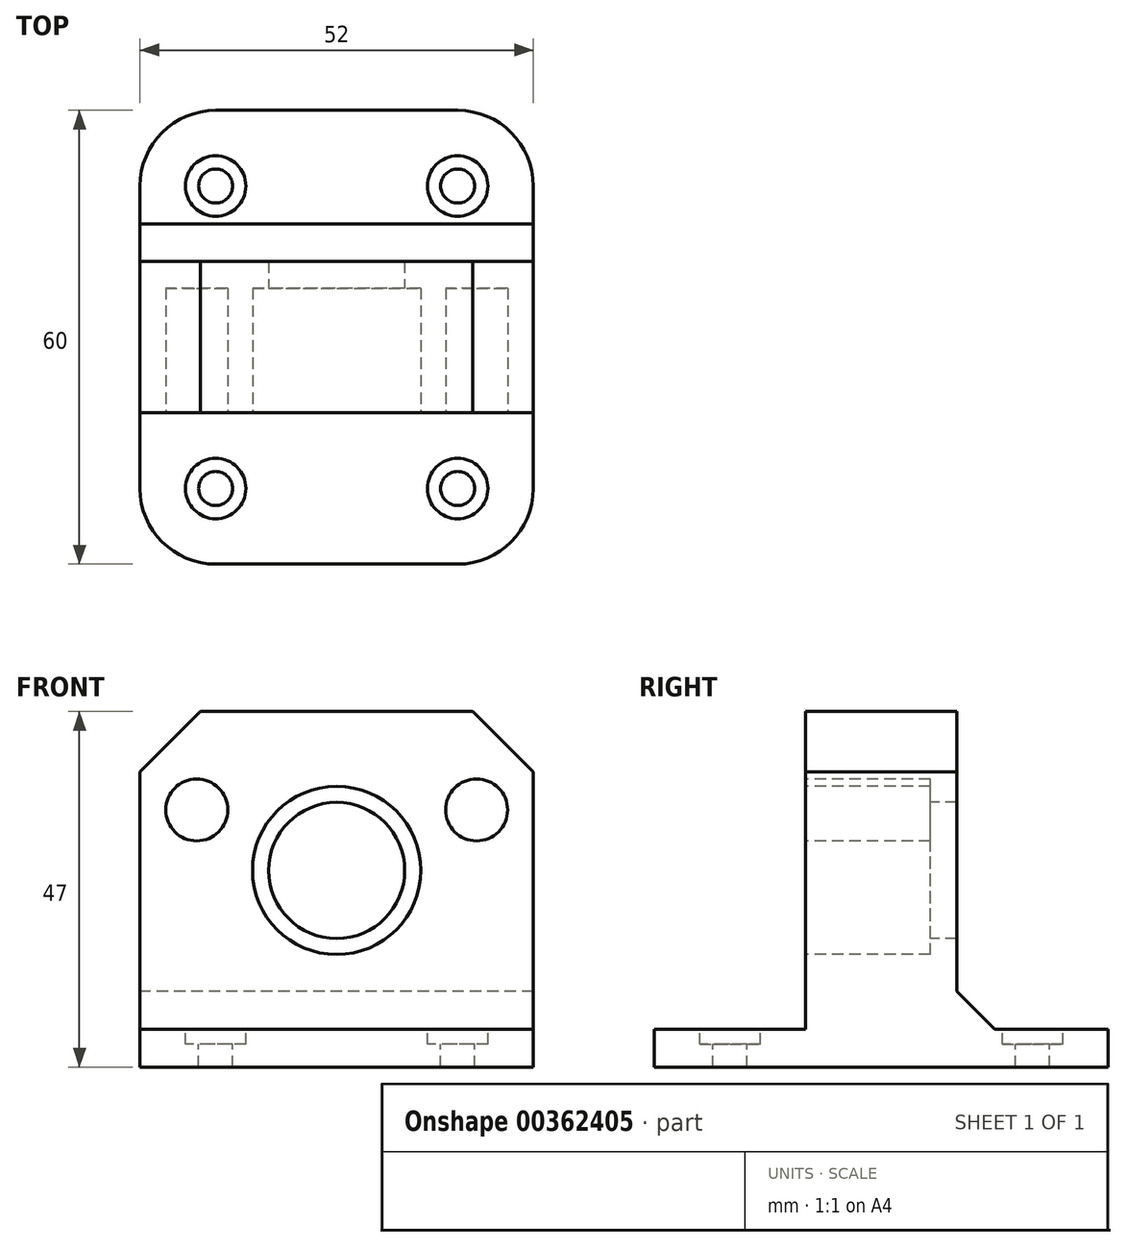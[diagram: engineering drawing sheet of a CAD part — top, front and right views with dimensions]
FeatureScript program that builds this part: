
annotation { "Feature Type Name" : "Feature", "Feature Type Description" : "" }
export const myFeature = defineFeature(function(context is Context, id is Id, definition is map)
    precondition{}
    {
        {
            var Q0;
            Q0=qCreatedBy(makeId("Front.planeOp"),FACE);
            var sketch = newSketch(context, id + "F0", { "sketchPlane" : qUnion([Q0])});
            skLineSegment(sketch, "E0.bottom", {"start": v(26, -21) * mm, "end": v(-26, -21) * mm});
            skLineSegment(sketch, "E0.top", {"start": v(26, 21) * mm, "end": v(-26, 21) * mm});
            skLineSegment(sketch, "E0.left", {"start": v(26, -21) * mm, "end": v(26, 21) * mm});
            skLineSegment(sketch, "E0.right", {"start": v(-26, -21) * mm, "end": v(-26, 21) * mm});
            skPoint(sketch, "E0.middle", {"position": v(0, 0) * mm});
            skSolve(sketch);
        }
        {
            var Q0;
            Q0=qSketchRegion(id+"F0",true);
            extrude(context, id + "F1", {"entities" : qUnion([Q0]), "endBound" : BoundingType.SYMMETRIC, "depth" : 20 * mm});
        }
        {
            var Q0;
            Q0=qCreatedBy(makeId("Front.planeOp"),FACE);
            var sketch = newSketch(context, id + "F2", { "sketchPlane" : qUnion([Q0])});
            skLineSegment(sketch, "E1.bottom", {"start": v(-26, -21) * mm, "end": v(26, -21) * mm});
            skLineSegment(sketch, "E1.top", {"start": v(-26, -26) * mm, "end": v(26, -26) * mm});
            skLineSegment(sketch, "E1.left", {"start": v(-26, -21) * mm, "end": v(-26, -26) * mm});
            skLineSegment(sketch, "E1.right", {"start": v(26, -21) * mm, "end": v(26, -26) * mm});
            skSolve(sketch);
        }
        {
            var Q0;
            Q0=qSketchRegion(id+"F2",true);
            extrude(context, id + "F3", {"entities" : qUnion([Q0]), "operationType" : NewBodyOperationType.ADD, "endBound" : BoundingType.SYMMETRIC, "depth" : 60 * mm});
        }
        {
            var Q0;
            Q0=makeQuery(id+"F1.opExtrude","CAP_FACE",FACE,{"disambiguationData":[OSD([sQuery(id+"F0.wireOp",EDGE,"E0.bottom"),sQuery(id+"F0.wireOp",EDGE,"E0.top"),sQuery(id+"F0.wireOp",EDGE,"E0.left"),sQuery(id+"F0.wireOp",EDGE,"E0.right")])],"isStart":false});
            var sketch = newSketch(context, id + "F4", { "sketchPlane" : qUnion([Q0])});
            skCircle(sketch, "E2", {"center": v(0, 0) * mm, "radius": 9 * mm});
            skSolve(sketch);
        }
        {
            var Q0;
            Q0=qSketchRegion(id+"F4",true);
            extrude(context, id + "F5", {"entities" : qUnion([Q0]), "operationType" : NewBodyOperationType.REMOVE, "endBound" : BoundingType.THROUGH_ALL, "oppositeDirection" : true, "depth" : 25 * mm});
        }
        {
            var Q0;
            Q0=makeQuery(id+"F1.opExtrude","CAP_FACE",FACE,{"disambiguationData":[OSD([sQuery(id+"F0.wireOp",EDGE,"E0.bottom"),sQuery(id+"F0.wireOp",EDGE,"E0.top"),sQuery(id+"F0.wireOp",EDGE,"E0.left"),sQuery(id+"F0.wireOp",EDGE,"E0.right")])],"isStart":false});
            var sketch = newSketch(context, id + "F6", { "sketchPlane" : qUnion([Q0])});
            skCircle(sketch, "E3", {"center": v(0, 0) * mm, "radius": 11.12 * mm});
            skCircle(sketch, "E4", {"center": v(-18.5, 8) * mm, "radius": 4.1 * mm});
            skCircle(sketch, "E5", {"center": v(18.5, 8) * mm, "radius": 4.1 * mm});
            skSolve(sketch);
        }
        {
            var Q0;
            Q0=qSketchRegion(id+"F6",true);
            extrude(context, id + "F7", {"entities" : qUnion([Q0]), "operationType" : NewBodyOperationType.REMOVE, "oppositeDirection" : true, "depth" : 16.5 * mm});
        }
        {
            var Q0;
            {var subQ2=sQuery(id+"F2.wireOp",EDGE,"E1.bottom");var subQ3=sQuery(id+"F0.wireOp",EDGE,"E0.right");var subQ4=sQuery(id+"F0.wireOp",EDGE,"E0.left");Q0=makeQuery(id+"F3.boolean.opBoolean","SPLIT",FACE,{"disambiguationData":[TD([makeQuery(id+"F1.opExtrude","CAP_FACE",FACE,{"disambiguationData":[OSD([sQuery(id+"F0.wireOp",EDGE,"E0.bottom"),sQuery(id+"F0.wireOp",EDGE,"E0.top"),subQ4,subQ3])],"isStart":false})])],"derivedFrom":makeQuery(id+"F3.opExtrude","SWEPT_FACE",FACE,{"disambiguationData":[OSD([subQ2])]})});}
            var sketch = newSketch(context, id + "F8", { "sketchPlane" : qUnion([Q0])});
            skCircle(sketch, "E6", {"center": v(-16, 20) * mm, "radius": 2.25 * mm});
            skCircle(sketch, "E7", {"center": v(16, 20) * mm, "radius": 2.25 * mm});
            skCircle(sketch, "E8", {"center": v(16, -20) * mm, "radius": 2.25 * mm});
            skCircle(sketch, "E9", {"center": v(-16, -20) * mm, "radius": 2.25 * mm});
            skSolve(sketch);
        }
        {
            var Q0;
            Q0=qSketchRegion(id+"F8",true);
            extrude(context, id + "F9", {"entities" : qUnion([Q0]), "operationType" : NewBodyOperationType.REMOVE, "endBound" : BoundingType.THROUGH_ALL, "oppositeDirection" : true, "depth" : 25 * mm});
        }
        {
            var Q0;
            {var subQ0=sQuery(id+"F0.wireOp",EDGE,"E0.right");var subQ1=sQuery(id+"F0.wireOp",EDGE,"E0.left");var subQ4=sQuery(id+"F2.wireOp",EDGE,"E1.bottom");Q0=makeQuery(id+"F3.boolean.opBoolean","SPLIT",FACE,{"disambiguationData":[TD([makeQuery(id+"F1.opExtrude","CAP_FACE",FACE,{"disambiguationData":[OSD([sQuery(id+"F0.wireOp",EDGE,"E0.bottom"),sQuery(id+"F0.wireOp",EDGE,"E0.top"),subQ1,subQ0])],"isStart":true})])],"derivedFrom":makeQuery(id+"F3.opExtrude","SWEPT_FACE",FACE,{"disambiguationData":[OSD([subQ4])]})});}
            var sketch = newSketch(context, id + "F10", { "sketchPlane" : qUnion([Q0])});
            skCircle(sketch, "E10", {"center": v(-16, 20) * mm, "radius": 4 * mm});
            skCircle(sketch, "E11", {"center": v(16, 20) * mm, "radius": 4 * mm});
            skCircle(sketch, "E12", {"center": v(-16, -20) * mm, "radius": 4 * mm});
            skCircle(sketch, "E13", {"center": v(16, -20) * mm, "radius": 4 * mm});
            skSolve(sketch);
        }
        {
            var Q0;
            Q0=qSketchRegion(id+"F10",true);
            extrude(context, id + "F11", {"entities" : qUnion([Q0]), "operationType" : NewBodyOperationType.REMOVE, "oppositeDirection" : true, "depth" : 2 * mm});
        }
        {
            var Q0;
            Q0=makeQuery(id+"F1.opExtrude","SWEPT_EDGE",EDGE,{"disambiguationData":[OSD([sQuery(id+"F0.wireOp",EDGE,"E0.top"),sQuery(id+"F0.wireOp",EDGE,"E0.right")])]});
            var Q1;
            Q1=makeQuery(id+"F1.opExtrude","SWEPT_EDGE",EDGE,{"disambiguationData":[OSD([sQuery(id+"F0.wireOp",EDGE,"E0.top"),sQuery(id+"F0.wireOp",EDGE,"E0.left")])]});
            chamfer(context, id + "F12", {"entities" : qUnion([Q0, Q1]), "width" : 8 * mm, "tangentPropagation" : true});
        }
        {
            var Q0;
            Q0=makeQuery(id+"F1.opExtrude","CAP_EDGE",EDGE,{"disambiguationData":[OSD([sQuery(id+"F0.wireOp",EDGE,"E0.bottom")])],"isStart":false});
            var Q1;
            Q1=makeQuery(id+"F1.opExtrude","CAP_EDGE",EDGE,{"disambiguationData":[OSD([sQuery(id+"F0.wireOp",EDGE,"E0.bottom")])],"isStart":true});
            chamfer(context, id + "F13", {"entities" : qUnion([Q0, Q1]), "width" : 5 * mm, "tangentPropagation" : true});
        }
        {
            var Q0;
            Q0=makeQuery(id+"F3.opExtrude","CAP_EDGE",EDGE,{"disambiguationData":[OSD([sQuery(id+"F2.wireOp",EDGE,"E1.right")])],"isStart":true});
            var Q1;
            Q1=makeQuery(id+"F3.opExtrude","CAP_EDGE",EDGE,{"disambiguationData":[OSD([sQuery(id+"F2.wireOp",EDGE,"E1.left")])],"isStart":true});
            var Q2;
            Q2=makeQuery(id+"F3.opExtrude","CAP_EDGE",EDGE,{"disambiguationData":[OSD([sQuery(id+"F2.wireOp",EDGE,"E1.right")])],"isStart":false});
            var Q3;
            Q3=makeQuery(id+"F3.opExtrude","CAP_EDGE",EDGE,{"disambiguationData":[OSD([sQuery(id+"F2.wireOp",EDGE,"E1.left")])],"isStart":false});
            fillet(context, id + "F14", {"entities" : qUnion([Q0, Q1, Q2, Q3]), "radius" : 10 * mm, "tangentPropagation" : true, "allowEdgeOverflow" : false});
        }
    });
